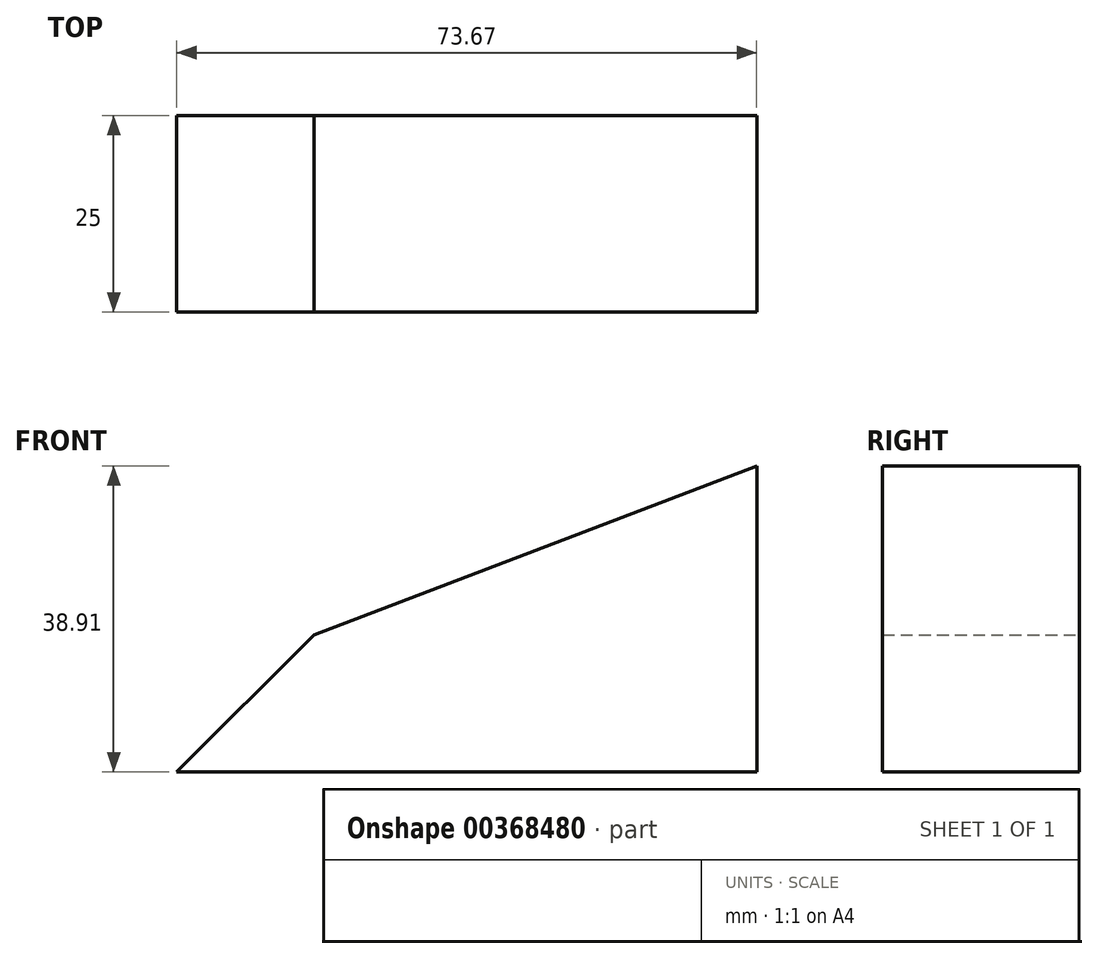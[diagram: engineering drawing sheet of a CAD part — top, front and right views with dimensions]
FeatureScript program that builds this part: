
annotation { "Feature Type Name" : "Feature", "Feature Type Description" : "" }
export const myFeature = defineFeature(function(context is Context, id is Id, definition is map)
    precondition{}
    {
        {
            var Q0;
            Q0=qCreatedBy(makeId("Front.planeOp"),FACE);
            var sketch = newSketch(context, id + "F0", { "sketchPlane" : qUnion([Q0])});
            skLineSegment(sketch, "E0.bottom", {"start": v(-106.36, 11.35) * mm, "end": v(-50.14, 32.8) * mm});
            skLineSegment(sketch, "E0.top", {"start": v(-123.8, -6.1) * mm, "end": v(-50.14, -6.1) * mm});
            skLineSegment(sketch, "E0.left", {"start": v(-106.36, 11.35) * mm, "end": v(-123.8, -6.1) * mm});
            skLineSegment(sketch, "E0.right", {"start": v(-50.14, 32.8) * mm, "end": v(-50.14, -6.1) * mm});
            skLineSegment(sketch, "E1", {"start": v(-139.73, 25.57) * mm, "end": v(-112.8, 49.28) * mm, "construction": true});
            skLineSegment(sketch, "E2", {"start": v(-112.8, 49.28) * mm, "end": v(-92.98, 43.02) * mm, "construction": true});
            skLineSegment(sketch, "E3", {"start": v(-92.98, 43.02) * mm, "end": v(-106.02, 24.73) * mm, "construction": true});
            skLineSegment(sketch, "E4", {"start": v(-106.02, 24.73) * mm, "end": v(-139.73, 25.57) * mm, "construction": true});
            skSolve(sketch);
        }
        {
            var Q0;
            Q0 = qSketchRegion(id + "F0", true);
            extrude(context, id + "F1", {"entities" : qUnion([Q0]), "depth" : 25 * mm});
        }
    });
